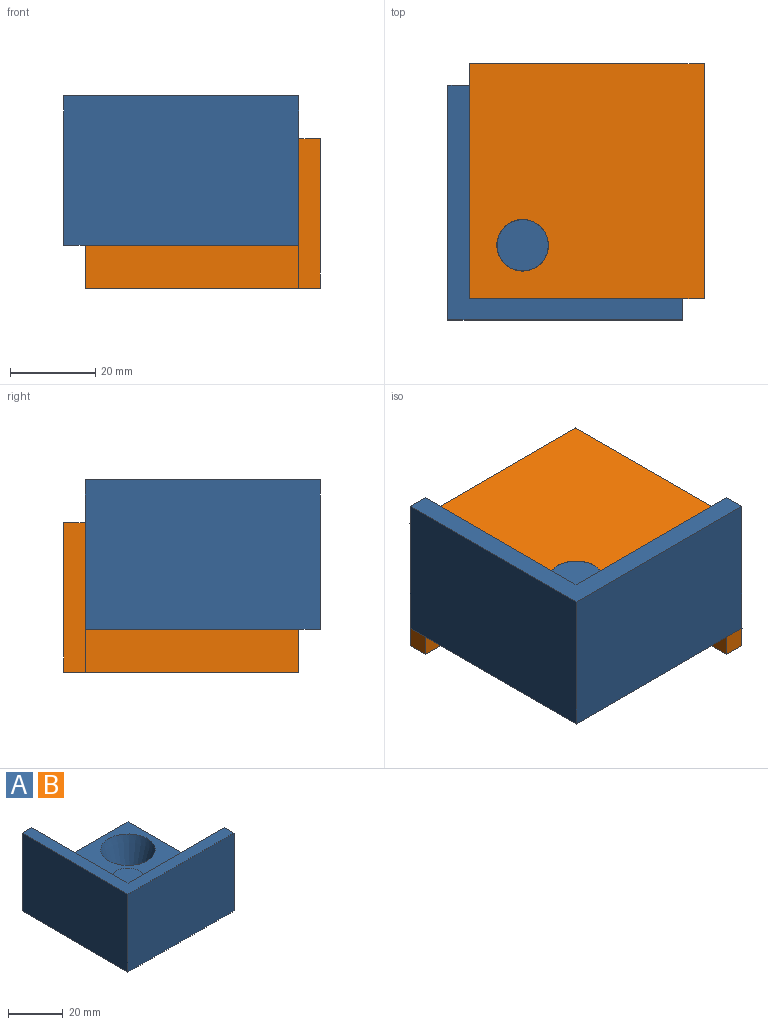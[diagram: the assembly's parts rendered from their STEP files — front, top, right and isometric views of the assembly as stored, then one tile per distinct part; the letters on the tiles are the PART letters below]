
ASSEMBLY  parts=2 mates=1
PART A: 12 faces, bbox 55x55x35 mm
  f0: plane 55x35mm, normal (1,0,0), area 800mm2, adj f1,f3,f4,f8,f10,f11
  f1: plane 55x35mm, normal (0,1,0), area 800mm2, adj f0,f3,f4,f7,f9,f11
  f2: cone r=10mm half-angle=17.5deg, axis (0,0,1), area 661.2mm2, adj f3,f4
  f3: plane 50x50mm, normal (0,0,1), area 1871.7mm2, adj f0,f1,f2,f6,f7,f8
  f4: plane 55x55mm, normal (0,0,-1), area 2909.7mm2, adj f0,f1,f2,f9,f10
  f5: plane 12x12mm, normal (0,0,1), area 113.1mm2, adj f6
  f6: cone r=6mm half-angle=17.7deg, axis (0,0,-1), area 659.7mm2, adj f3,f5
  f7: plane 50x22.5mm, normal (1,0,0), area 1125mm2, adj f1,f3,f8,f11
  f8: plane 50x22.5mm, normal (0,1,0), area 1125mm2, adj f0,f3,f7,f11
  f9: plane 55x35mm, normal (-1,0,0), area 1925mm2, adj f1,f4,f10,f11
  f10: plane 55x35mm, normal (0,-1,0), area 1925mm2, adj f0,f4,f9,f11
  f11: plane 55x55mm, normal (0,0,1), area 525mm2, adj f0,f1,f7,f8,f9,f10
PART B: same geometry as A
PLACE A rot(axis=(0.58,-0.64,0.5),0deg) t=(22.64,20.43,17.87)mm
PLACE B rot(axis=(-0.71,0.71,0),180deg) t=(72.64,70.43,42.87)mm
MATE fastened B.f2 <-> A.f6  axis (0,0,-1) through (35.14,32.93,30.37)mm
